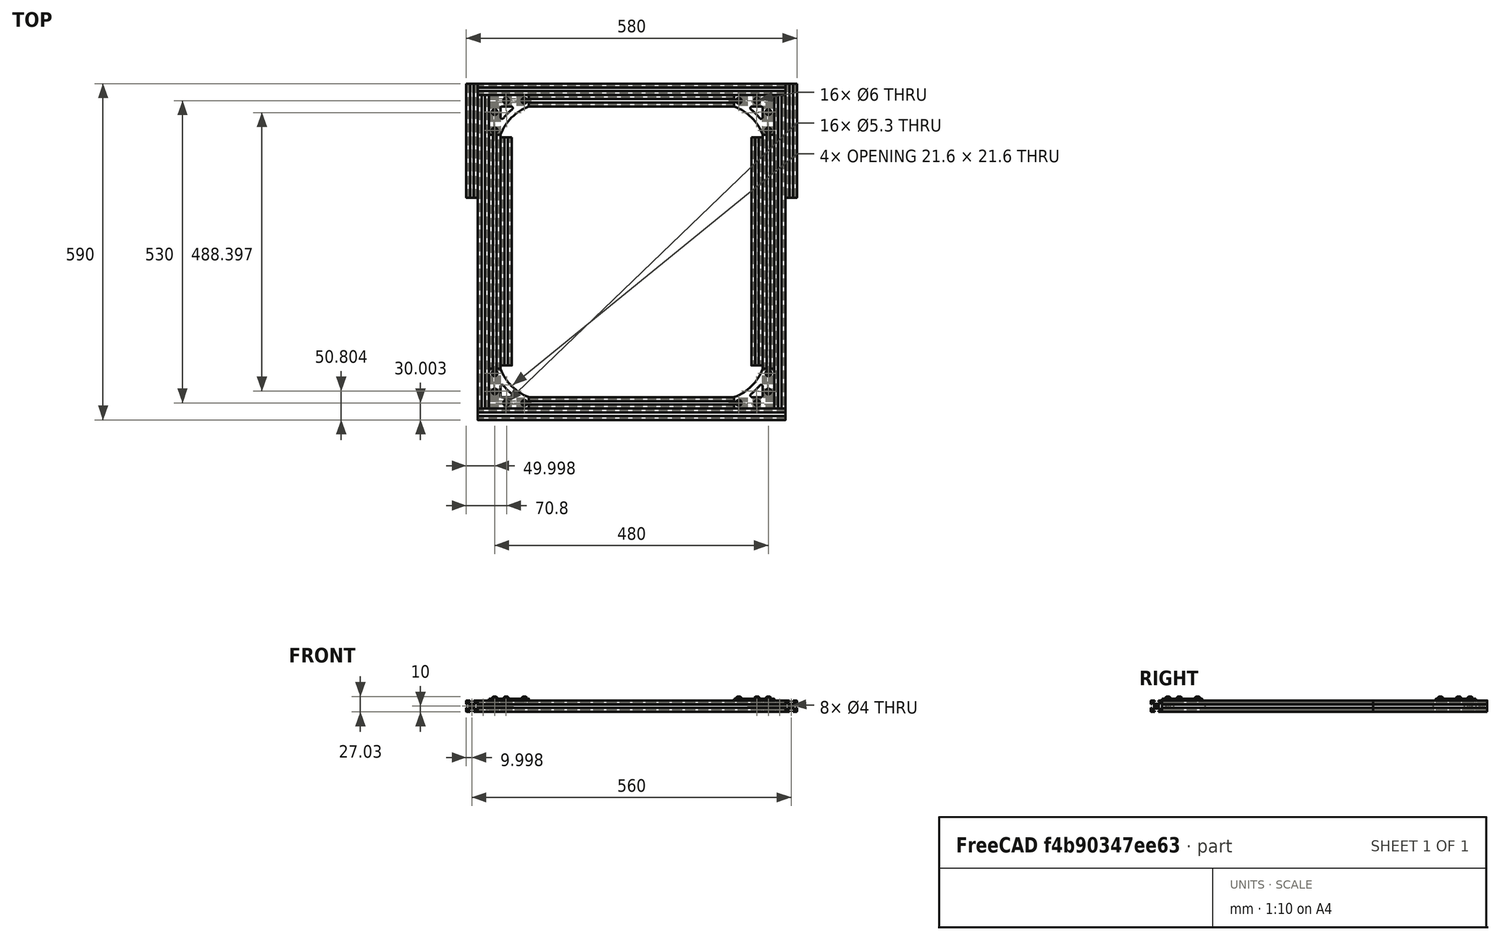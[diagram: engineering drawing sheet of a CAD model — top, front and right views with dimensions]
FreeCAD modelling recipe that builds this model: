
FCSTD DOCUMENT  (FreeCAD 0.17R7761 (Git))
Label: TAZ6_frame_assy_fixture
License: CreativeCommons Attribution-ShareAlike
LicenseURL: http://creativecommons.org/licenses/by-sa/4.0/
objects: App::FeaturePython×89, Part::FeaturePython×49, Spreadsheet::Sheet×1
note: 49 computed .brp shape members not serialized (recipe doc carries the construction recipe); baked Part::Feature solids carry a one-line shape summary decoded from their .brp

FEATURE [Part::FeaturePython] _00mm_extrusion_01  # a2plus imported part (geometry in sourceFile) (typed FeaturePython)
  Placement = pos=(17.428,58.3428,0) rot=(0.57735,0.57735,0.57735;2.0944rad)
  fixedPosition = true
  sourceFile = <userpath>/shared-j/devel/lulzbot/TAZ/Olive/production_parts/jigs/500mm_extrusion.fcstd
  timeLastImport = 1465231095
  updateColors = true
FEATURE [Part::FeaturePython] _10mm_extrusion_01  # a2plus imported part (geometry in sourceFile) (typed FeaturePython)
  Placement = pos=(7.42801,68.3428,0) rot=(1,0,0;1.5708rad)
  fixedPosition = false
  sourceFile = <userpath>/shared-j/devel/lulzbot/TAZ/Olive/production_parts/jigs/510mm_extrusion.fcstd
  timeLastImport = 1465230221
  updateColors = true
FEATURE [App::FeaturePython] planeConstraint01  # a2plus constraint (typed FeaturePython)
  Object1 = _10mm_extrusion_01
  Object2 = _00mm_extrusion_01
  SubElement1 = Face2
  SubElement2 = Face27
  Type = plane
  directionConstraint = 0
  offset = 0
FEATURE [App::FeaturePython] planeConstraint01_mirror  label="planeConstraint01_"  # a2plus constraint (typed FeaturePython)
  Object1 = _10mm_extrusion_01
  Object2 = _00mm_extrusion_01
  SubElement1 = Face2
  SubElement2 = Face27
  Type = plane
  directionConstraint = 0
  offset = 0
FEATURE [App::FeaturePython] planeConstraint02  # a2plus constraint (typed FeaturePython)
  Object1 = _00mm_extrusion_01
  Object2 = _10mm_extrusion_01
  SubElement1 = Face2
  SubElement2 = Face27
  Type = plane
  directionConstraint = 1
  offset = 0
FEATURE [App::FeaturePython] planeConstraint02_mirror  label="planeConstraint02_"  # a2plus constraint (typed FeaturePython)
  Object1 = _00mm_extrusion_01
  Object2 = _10mm_extrusion_01
  SubElement1 = Face2
  SubElement2 = Face27
  Type = plane
  directionConstraint = 1
  offset = 0
FEATURE [Part::FeaturePython] _10mm_extrusion_01001  # a2plus imported part (geometry in sourceFile) (typed FeaturePython)
  Placement = pos=(-472.572,68.3428,0) rot=(1,0,0;1.5708rad)
  fixedPosition = false
  sourceFile = <userpath>/shared-j/devel/lulzbot/TAZ/Olive/production_parts/jigs/510mm_extrusion.fcstd
  timeLastImport = 1465230221
  updateColors = true
FEATURE [App::FeaturePython] planeConstraint03  # a2plus constraint (typed FeaturePython)
  Object1 = _10mm_extrusion_01001
  Object2 = _00mm_extrusion_01
  SubElement1 = Face1
  SubElement2 = Face23
  Type = plane
  directionConstraint = 0
  offset = 0
FEATURE [App::FeaturePython] planeConstraint03_mirror  label="planeConstraint03_"  # a2plus constraint (typed FeaturePython)
  Object1 = _10mm_extrusion_01001
  Object2 = _00mm_extrusion_01
  SubElement1 = Face1
  SubElement2 = Face23
  Type = plane
  directionConstraint = 0
  offset = 0
FEATURE [App::FeaturePython] planeConstraint04  # a2plus constraint (typed FeaturePython)
  Object1 = _10mm_extrusion_01001
  Object2 = _00mm_extrusion_01
  SubElement1 = Face6
  SubElement2 = Face5
  Type = plane
  directionConstraint = 0
  offset = 0
FEATURE [App::FeaturePython] planeConstraint04_mirror  label="planeConstraint04_"  # a2plus constraint (typed FeaturePython)
  Object1 = _10mm_extrusion_01001
  Object2 = _00mm_extrusion_01
  SubElement1 = Face6
  SubElement2 = Face5
  Type = plane
  directionConstraint = 0
  offset = 0
FEATURE [App::FeaturePython] planeConstraint05  # a2plus constraint (typed FeaturePython)
  Object1 = _10mm_extrusion_01001
  Object2 = _00mm_extrusion_01
  SubElement1 = Face2
  SubElement2 = Face27
  Type = plane
  directionConstraint = 0
  offset = 0
FEATURE [App::FeaturePython] planeConstraint05_mirror  label="planeConstraint05_"  # a2plus constraint (typed FeaturePython)
  Object1 = _10mm_extrusion_01001
  Object2 = _00mm_extrusion_01
  SubElement1 = Face2
  SubElement2 = Face27
  Type = plane
  directionConstraint = 0
  offset = 0
FEATURE [Part::FeaturePython] _00mm_extrusion_01001  # a2plus imported part (geometry in sourceFile) (typed FeaturePython)
  Placement = pos=(17.428,588.343,0) rot=(0.57735,0.57735,0.57735;2.0944rad)
  fixedPosition = false
  sourceFile = <userpath>/shared-j/devel/lulzbot/TAZ/Olive/production_parts/jigs/500mm_extrusion.fcstd
  timeLastImport = 1465231095
  updateColors = true
FEATURE [App::FeaturePython] planeConstraint06  # a2plus constraint (typed FeaturePython)
  Object1 = _00mm_extrusion_01001
  Object2 = _10mm_extrusion_01001
  SubElement1 = Face5
  SubElement2 = Face26
  Type = plane
  directionConstraint = 0
  offset = 0
FEATURE [App::FeaturePython] planeConstraint06_mirror  label="planeConstraint06_"  # a2plus constraint (typed FeaturePython)
  Object1 = _00mm_extrusion_01001
  Object2 = _10mm_extrusion_01001
  SubElement1 = Face5
  SubElement2 = Face26
  Type = plane
  directionConstraint = 0
  offset = 0
FEATURE [App::FeaturePython] planeConstraint07  # a2plus constraint (typed FeaturePython)
  Object1 = _00mm_extrusion_01001
  Object2 = _10mm_extrusion_01001
  SubElement1 = Face6
  SubElement2 = Face5
  Type = plane
  directionConstraint = 1
  offset = 0
FEATURE [App::FeaturePython] planeConstraint07_mirror  label="planeConstraint07_"  # a2plus constraint (typed FeaturePython)
  Object1 = _00mm_extrusion_01001
  Object2 = _10mm_extrusion_01001
  SubElement1 = Face6
  SubElement2 = Face5
  Type = plane
  directionConstraint = 1
  offset = 0
FEATURE [App::FeaturePython] planeConstraint08  # a2plus constraint (typed FeaturePython)
  Object1 = _00mm_extrusion_01001
  Object2 = _10mm_extrusion_01001
  SubElement1 = Face1
  SubElement2 = Face23
  Type = plane
  directionConstraint = 0
  offset = 0
FEATURE [App::FeaturePython] planeConstraint08_mirror  label="planeConstraint08_"  # a2plus constraint (typed FeaturePython)
  Object1 = _00mm_extrusion_01001
  Object2 = _10mm_extrusion_01001
  SubElement1 = Face1
  SubElement2 = Face23
  Type = plane
  directionConstraint = 0
  offset = 0
FEATURE [Part::FeaturePython] muxedAssembly  label="TAZ6_frame_muxedAssembly"  # WARN: FeaturePython — macro-defined, semantics opaque (R4)
  type = muxedAssembly
FEATURE [Part::FeaturePython] _50mm_extrusion_01  # a2plus imported part (geometry in sourceFile) (typed FeaturePython)
  Placement = pos=(-492.572,48.3428,0) rot=(1,0,0;1.5708rad)
  fixedPosition = false
  sourceFile = <userpath>/shared-j/devel/lulzbot/TAZ/Olive/production_parts/jigs/550mm_extrusion.fcstd
  timeLastImport = 1465233027
  updateColors = true
FEATURE [App::FeaturePython] planeConstraint09  # a2plus constraint (typed FeaturePython)
  Object1 = _50mm_extrusion_01
  Object2 = muxedAssembly
  SubElement1 = Face23
  SubElement2 = Face23
  Type = plane
  directionConstraint = 0
  offset = 0
FEATURE [App::FeaturePython] planeConstraint09_mirror  label="planeConstraint09_"  # a2plus constraint (typed FeaturePython)
  Object1 = _50mm_extrusion_01
  Object2 = muxedAssembly
  SubElement1 = Face23
  SubElement2 = Face23
  Type = plane
  directionConstraint = 0
  offset = 0
FEATURE [App::FeaturePython] planeConstraint10  # a2plus constraint (typed FeaturePython)
  Object1 = _50mm_extrusion_01
  Object2 = muxedAssembly
  SubElement1 = Face2
  SubElement2 = Face6
  Type = plane
  directionConstraint = 1
  offset = 0
FEATURE [App::FeaturePython] planeConstraint10_mirror  label="planeConstraint10_"  # a2plus constraint (typed FeaturePython)
  Object1 = _50mm_extrusion_01
  Object2 = muxedAssembly
  SubElement1 = Face2
  SubElement2 = Face6
  Type = plane
  directionConstraint = 1
  offset = 0
FEATURE [App::FeaturePython] planeConstraint11  # a2plus constraint (typed FeaturePython)
  Object1 = _50mm_extrusion_01
  Object2 = muxedAssembly
  SubElement1 = Face47
  SubElement2 = Face108
  Type = plane
  directionConstraint = 1
  offset = 0
FEATURE [App::FeaturePython] planeConstraint11_mirror  label="planeConstraint11_"  # a2plus constraint (typed FeaturePython)
  Object1 = _50mm_extrusion_01
  Object2 = muxedAssembly
  SubElement1 = Face47
  SubElement2 = Face108
  Type = plane
  directionConstraint = 1
  offset = 0
FEATURE [Part::FeaturePython] _50mm_extrusion_01001  # a2plus imported part (geometry in sourceFile) (typed FeaturePython)
  Placement = pos=(27.428,598.343,0) rot=(0,0.707107,0.707107;3.14159rad)
  fixedPosition = false
  sourceFile = <userpath>/shared-j/devel/lulzbot/TAZ/Olive/production_parts/jigs/550mm_extrusion.fcstd
  timeLastImport = 1465233027
  updateColors = true
FEATURE [App::FeaturePython] planeConstraint12  # a2plus constraint (typed FeaturePython)
  Object1 = _50mm_extrusion_01001
  Object2 = muxedAssembly
  SubElement1 = Face23
  SubElement2 = Face74
  Type = plane
  directionConstraint = 0
  offset = 0
FEATURE [App::FeaturePython] planeConstraint12_mirror  label="planeConstraint12_"  # a2plus constraint (typed FeaturePython)
  Object1 = _50mm_extrusion_01001
  Object2 = muxedAssembly
  SubElement1 = Face23
  SubElement2 = Face74
  Type = plane
  directionConstraint = 0
  offset = 0
FEATURE [App::FeaturePython] planeConstraint13  # a2plus constraint (typed FeaturePython)
  Object1 = _50mm_extrusion_01001
  Object2 = muxedAssembly
  SubElement1 = Face47
  SubElement2 = Face98
  Type = plane
  directionConstraint = 1
  offset = 0
FEATURE [App::FeaturePython] planeConstraint13_mirror  label="planeConstraint13_"  # a2plus constraint (typed FeaturePython)
  Object1 = _50mm_extrusion_01001
  Object2 = muxedAssembly
  SubElement1 = Face47
  SubElement2 = Face98
  Type = plane
  directionConstraint = 1
  offset = 0
FEATURE [App::FeaturePython] planeConstraint14  # a2plus constraint (typed FeaturePython)
  Object1 = _50mm_extrusion_01001
  Object2 = muxedAssembly
  SubElement1 = Face2
  SubElement2 = Face200
  Type = plane
  directionConstraint = 1
  offset = 0
FEATURE [App::FeaturePython] planeConstraint14_mirror  label="planeConstraint14_"  # a2plus constraint (typed FeaturePython)
  Object1 = _50mm_extrusion_01001
  Object2 = muxedAssembly
  SubElement1 = Face2
  SubElement2 = Face200
  Type = plane
  directionConstraint = 1
  offset = 0
FEATURE [Part::FeaturePython] _40mm_extrusion_01  # a2plus imported part (geometry in sourceFile) (typed FeaturePython)
  Placement = pos=(37.428,38.3428,0) rot=(0.57735,0.57735,0.57735;2.0944rad)
  fixedPosition = false
  sourceFile = <userpath>/shared-j/devel/lulzbot/TAZ/Olive/production_parts/jigs/540mm_extrusion.fcstd
  timeLastImport = 1465233682
  updateColors = true
FEATURE [App::FeaturePython] planeConstraint15  # a2plus constraint (typed FeaturePython)
  Object1 = _40mm_extrusion_01
  Object2 = muxedAssembly
  SubElement1 = Face23
  SubElement2 = Face23
  Type = plane
  directionConstraint = 0
  offset = 0
FEATURE [App::FeaturePython] planeConstraint15_mirror  label="planeConstraint15_"  # a2plus constraint (typed FeaturePython)
  Object1 = _40mm_extrusion_01
  Object2 = muxedAssembly
  SubElement1 = Face23
  SubElement2 = Face23
  Type = plane
  directionConstraint = 0
  offset = 0
FEATURE [App::FeaturePython] planeConstraint16  # a2plus constraint (typed FeaturePython)
  Object1 = _40mm_extrusion_01
  Object2 = muxedAssembly
  SubElement1 = Face27
  SubElement2 = Face6
  Type = plane
  directionConstraint = 1
  offset = 0
FEATURE [App::FeaturePython] planeConstraint16_mirror  label="planeConstraint16_"  # a2plus constraint (typed FeaturePython)
  Object1 = _40mm_extrusion_01
  Object2 = muxedAssembly
  SubElement1 = Face27
  SubElement2 = Face6
  Type = plane
  directionConstraint = 1
  offset = 0
FEATURE [App::FeaturePython] planeConstraint17  # a2plus constraint (typed FeaturePython)
  Object1 = _40mm_extrusion_01
  Object2 = _50mm_extrusion_01
  SubElement1 = Face5
  SubElement2 = Face6
  Type = plane
  directionConstraint = 0
  offset = 0
FEATURE [App::FeaturePython] planeConstraint17_mirror  label="planeConstraint17_"  # a2plus constraint (typed FeaturePython)
  Object1 = _40mm_extrusion_01
  Object2 = _50mm_extrusion_01
  SubElement1 = Face5
  SubElement2 = Face6
  Type = plane
  directionConstraint = 0
  offset = 0
FEATURE [Part::FeaturePython] _40mm_extrusion_01001  # a2plus imported part (geometry in sourceFile) (typed FeaturePython)
  Placement = pos=(37.428,608.343,0) rot=(0.57735,0.57735,0.57735;2.0944rad)
  fixedPosition = false
  sourceFile = <userpath>/shared-j/devel/lulzbot/TAZ/Olive/production_parts/jigs/540mm_extrusion.fcstd
  timeLastImport = 1465233682
  updateColors = true
FEATURE [App::FeaturePython] planeConstraint18  # a2plus constraint (typed FeaturePython)
  Object1 = _40mm_extrusion_01001
  Object2 = _50mm_extrusion_01001
  SubElement1 = Face1
  SubElement2 = Face1
  Type = plane
  directionConstraint = 0
  offset = 0
FEATURE [App::FeaturePython] planeConstraint18_mirror  label="planeConstraint18_"  # a2plus constraint (typed FeaturePython)
  Object1 = _40mm_extrusion_01001
  Object2 = _50mm_extrusion_01001
  SubElement1 = Face1
  SubElement2 = Face1
  Type = plane
  directionConstraint = 0
  offset = 0
FEATURE [App::FeaturePython] planeConstraint19  # a2plus constraint (typed FeaturePython)
  Object1 = _40mm_extrusion_01001
  Object2 = _50mm_extrusion_01001
  SubElement1 = Face2
  SubElement2 = Face26
  Type = plane
  directionConstraint = 1
  offset = 0
FEATURE [App::FeaturePython] planeConstraint19_mirror  label="planeConstraint19_"  # a2plus constraint (typed FeaturePython)
  Object1 = _40mm_extrusion_01001
  Object2 = _50mm_extrusion_01001
  SubElement1 = Face2
  SubElement2 = Face26
  Type = plane
  directionConstraint = 1
  offset = 0
FEATURE [App::FeaturePython] planeConstraint20  # a2plus constraint (typed FeaturePython)
  Object1 = _40mm_extrusion_01001
  Object2 = _50mm_extrusion_01001
  SubElement1 = Face6
  SubElement2 = Face2
  Type = plane
  directionConstraint = 0
  offset = 0
FEATURE [App::FeaturePython] planeConstraint20_mirror  label="planeConstraint20_"  # a2plus constraint (typed FeaturePython)
  Object1 = _40mm_extrusion_01001
  Object2 = _50mm_extrusion_01001
  SubElement1 = Face6
  SubElement2 = Face2
  Type = plane
  directionConstraint = 0
  offset = 0
FEATURE [Part::FeaturePython] _00mm_extrusion_01002  # a2plus imported part (geometry in sourceFile) (typed FeaturePython)
  Placement = pos=(47.428,618.343,0) rot=(0,0.707107,0.707107;3.14159rad)
  fixedPosition = false
  sourceFile = <userpath>/shared-j/devel/lulzbot/TAZ/Olive/production_parts/jigs/200mm_extrusion.fcstd
  timeLastImport = 1465234395
  updateColors = true
FEATURE [App::FeaturePython] planeConstraint21  # a2plus constraint (typed FeaturePython)
  Object1 = _00mm_extrusion_01002
  Object2 = _40mm_extrusion_01001
  SubElement1 = Face50
  SubElement2 = Face50
  Type = plane
  directionConstraint = 0
  offset = 0
FEATURE [App::FeaturePython] planeConstraint21_mirror  label="planeConstraint21_"  # a2plus constraint (typed FeaturePython)
  Object1 = _00mm_extrusion_01002
  Object2 = _40mm_extrusion_01001
  SubElement1 = Face50
  SubElement2 = Face50
  Type = plane
  directionConstraint = 0
  offset = 0
FEATURE [App::FeaturePython] planeConstraint22  # a2plus constraint (typed FeaturePython)
  Object1 = _00mm_extrusion_01002
  Object2 = _40mm_extrusion_01001
  SubElement1 = Face2
  SubElement2 = Face27
  Type = plane
  directionConstraint = 1
  offset = 0
FEATURE [App::FeaturePython] planeConstraint22_mirror  label="planeConstraint22_"  # a2plus constraint (typed FeaturePython)
  Object1 = _00mm_extrusion_01002
  Object2 = _40mm_extrusion_01001
  SubElement1 = Face2
  SubElement2 = Face27
  Type = plane
  directionConstraint = 1
  offset = 0
FEATURE [App::FeaturePython] planeConstraint23  # a2plus constraint (typed FeaturePython)
  Object1 = _00mm_extrusion_01002
  Object2 = _50mm_extrusion_01001
  SubElement1 = Face27
  SubElement2 = Face26
  Type = plane
  directionConstraint = 0
  offset = 0
FEATURE [App::FeaturePython] planeConstraint23_mirror  label="planeConstraint23_"  # a2plus constraint (typed FeaturePython)
  Object1 = _00mm_extrusion_01002
  Object2 = _50mm_extrusion_01001
  SubElement1 = Face27
  SubElement2 = Face26
  Type = plane
  directionConstraint = 0
  offset = 0
FEATURE [Part::FeaturePython] _00mm_extrusion_01003  # a2plus imported part (geometry in sourceFile) (typed FeaturePython)
  Placement = pos=(-512.572,418.343,0) rot=(1,0,0;1.5708rad)
  fixedPosition = false
  sourceFile = <userpath>/shared-j/devel/lulzbot/TAZ/Olive/production_parts/jigs/200mm_extrusion.fcstd
  timeLastImport = 1465234395
  updateColors = true
FEATURE [App::FeaturePython] planeConstraint24  # a2plus constraint (typed FeaturePython)
  Object1 = _00mm_extrusion_01003
  Object2 = _50mm_extrusion_01
  SubElement1 = Face50
  SubElement2 = Face30
  Type = plane
  directionConstraint = 0
  offset = 0
FEATURE [App::FeaturePython] planeConstraint24_mirror  label="planeConstraint24_"  # a2plus constraint (typed FeaturePython)
  Object1 = _00mm_extrusion_01003
  Object2 = _50mm_extrusion_01
  SubElement1 = Face50
  SubElement2 = Face30
  Type = plane
  directionConstraint = 0
  offset = 0
FEATURE [App::FeaturePython] planeConstraint25  # a2plus constraint (typed FeaturePython)
  Object1 = _00mm_extrusion_01003
  Object2 = _40mm_extrusion_01001
  SubElement1 = Face5
  SubElement2 = Face27
  Type = plane
  directionConstraint = 0
  offset = 0
FEATURE [App::FeaturePython] planeConstraint25_mirror  label="planeConstraint25_"  # a2plus constraint (typed FeaturePython)
  Object1 = _00mm_extrusion_01003
  Object2 = _40mm_extrusion_01001
  SubElement1 = Face5
  SubElement2 = Face27
  Type = plane
  directionConstraint = 0
  offset = 0
FEATURE [App::FeaturePython] planeConstraint26  # a2plus constraint (typed FeaturePython)
  Object1 = _00mm_extrusion_01003
  Object2 = _50mm_extrusion_01
  SubElement1 = Face47
  SubElement2 = Face26
  Type = plane
  directionConstraint = 0
  offset = 0
FEATURE [App::FeaturePython] planeConstraint26_mirror  label="planeConstraint26_"  # a2plus constraint (typed FeaturePython)
  Object1 = _00mm_extrusion_01003
  Object2 = _50mm_extrusion_01
  SubElement1 = Face47
  SubElement2 = Face26
  Type = plane
  directionConstraint = 0
  offset = 0
FEATURE [Part::FeaturePython] _00mm_extrusion_01004  # a2plus imported part (geometry in sourceFile) (typed FeaturePython)
  Placement = pos=(-12.572,523.9,0) rot=(0,0.707107,0.707107;3.14159rad)
  fixedPosition = false
  sourceFile = <userpath>/shared-j/devel/lulzbot/TAZ/Olive/production_parts/jigs/400mm_extrusion.fcstd
  timeLastImport = 1465243496
  updateColors = true
FEATURE [App::FeaturePython] planeConstraint27  # a2plus constraint (typed FeaturePython)
  Object1 = _00mm_extrusion_01004
  Object2 = _50mm_extrusion_01001
  SubElement1 = Face50
  SubElement2 = Face50
  Type = plane
  directionConstraint = 0
  offset = 0
FEATURE [App::FeaturePython] planeConstraint27_mirror  label="planeConstraint27_"  # a2plus constraint (typed FeaturePython)
  Object1 = _00mm_extrusion_01004
  Object2 = _50mm_extrusion_01001
  SubElement1 = Face50
  SubElement2 = Face50
  Type = plane
  directionConstraint = 0
  offset = 0
FEATURE [App::FeaturePython] planeConstraint28  # a2plus constraint (typed FeaturePython)
  Object1 = _00mm_extrusion_01004
  Object2 = muxedAssembly
  SubElement1 = Face26
  SubElement2 = Face77
  Type = plane
  directionConstraint = 1
  offset = 0
FEATURE [App::FeaturePython] planeConstraint28_mirror  label="planeConstraint28_"  # a2plus constraint (typed FeaturePython)
  Object1 = _00mm_extrusion_01004
  Object2 = muxedAssembly
  SubElement1 = Face26
  SubElement2 = Face77
  Type = plane
  directionConstraint = 1
  offset = 0
FEATURE [Part::FeaturePython] _00mm_extrusion_01005  # a2plus imported part (geometry in sourceFile) (typed FeaturePython)
  Placement = pos=(-452.572,123.9,0) rot=(1,0,0;1.5708rad)
  fixedPosition = false
  sourceFile = <userpath>/shared-j/devel/lulzbot/TAZ/Olive/production_parts/jigs/400mm_extrusion.fcstd
  timeLastImport = 1465243496
  updateColors = true
FEATURE [App::FeaturePython] planeConstraint29  # a2plus constraint (typed FeaturePython)
  Object1 = _00mm_extrusion_01005
  Object2 = _50mm_extrusion_01
  SubElement1 = Face23
  SubElement2 = Face23
  Type = plane
  directionConstraint = 0
  offset = 0
FEATURE [App::FeaturePython] planeConstraint29_mirror  label="planeConstraint29_"  # a2plus constraint (typed FeaturePython)
  Object1 = _00mm_extrusion_01005
  Object2 = _50mm_extrusion_01
  SubElement1 = Face23
  SubElement2 = Face23
  Type = plane
  directionConstraint = 0
  offset = 0
FEATURE [App::FeaturePython] planeConstraint30  # a2plus constraint (typed FeaturePython)
  Object1 = _00mm_extrusion_01005
  Object2 = muxedAssembly
  SubElement1 = Face6
  SubElement2 = Face129
  Type = plane
  directionConstraint = 1
  offset = 0
FEATURE [App::FeaturePython] planeConstraint30_mirror  label="planeConstraint30_"  # a2plus constraint (typed FeaturePython)
  Object1 = _00mm_extrusion_01005
  Object2 = muxedAssembly
  SubElement1 = Face6
  SubElement2 = Face129
  Type = plane
  directionConstraint = 1
  offset = 0
FEATURE [App::FeaturePython] planeConstraint31  # a2plus constraint (typed FeaturePython)
  Object1 = _00mm_extrusion_01005
  Object2 = _00mm_extrusion_01004
  SubElement1 = Face2
  SubElement2 = Face5
  Type = plane
  directionConstraint = 0
  offset = 0
FEATURE [App::FeaturePython] planeConstraint31_mirror  label="planeConstraint31_"  # a2plus constraint (typed FeaturePython)
  Object1 = _00mm_extrusion_01005
  Object2 = _00mm_extrusion_01004
  SubElement1 = Face2
  SubElement2 = Face5
  Type = plane
  directionConstraint = 0
  offset = 0
FEATURE [Part::FeaturePython] corner_bracket_v2_0_PP_MP0106_step1_01  # a2plus imported part (geometry in sourceFile) (typed FeaturePython)
  Placement = pos=(-482.572,118.343,13.175) rot=(1,0,0;1.5708rad)
  fixedPosition = false
  sourceFile = <userpath>/shared-j/devel/lulzbot/TAZ/Olive/production_parts/machined_parts/corner_bracket_v2.0/corner_bracket_v2.0_PP-MP0106.step
  timeLastImport = 1441125151
  updateColors = true
FEATURE [App::FeaturePython] planeConstraint32  # a2plus constraint (typed FeaturePython)
  Object1 = corner_bracket_v2_0_PP_MP0106_step1_01
  Object2 = muxedAssembly
  SubElement1 = Face22
  SubElement2 = Face103
  Type = plane
  directionConstraint = 1
  offset = 0
FEATURE [App::FeaturePython] planeConstraint32_mirror  label="planeConstraint32_"  # a2plus constraint (typed FeaturePython)
  Object1 = corner_bracket_v2_0_PP_MP0106_step1_01
  Object2 = muxedAssembly
  SubElement1 = Face22
  SubElement2 = Face103
  Type = plane
  directionConstraint = 1
  offset = 0
FEATURE [App::FeaturePython] planeConstraint33  # a2plus constraint (typed FeaturePython)
  Object1 = corner_bracket_v2_0_PP_MP0106_step1_01
  Object2 = muxedAssembly
  SubElement1 = Face6
  SubElement2 = Face6
  Type = plane
  directionConstraint = 0
  offset = 0
FEATURE [App::FeaturePython] planeConstraint33_mirror  label="planeConstraint33_"  # a2plus constraint (typed FeaturePython)
  Object1 = corner_bracket_v2_0_PP_MP0106_step1_01
  Object2 = muxedAssembly
  SubElement1 = Face6
  SubElement2 = Face6
  Type = plane
  directionConstraint = 0
  offset = 0
FEATURE [App::FeaturePython] planeConstraint34  # a2plus constraint (typed FeaturePython)
  Object1 = corner_bracket_v2_0_PP_MP0106_step1_01
  Object2 = muxedAssembly
  SubElement1 = Face10
  SubElement2 = Face108
  Type = plane
  directionConstraint = 0
  offset = 0
FEATURE [App::FeaturePython] planeConstraint34_mirror  label="planeConstraint34_"  # a2plus constraint (typed FeaturePython)
  Object1 = corner_bracket_v2_0_PP_MP0106_step1_01
  Object2 = muxedAssembly
  SubElement1 = Face10
  SubElement2 = Face108
  Type = plane
  directionConstraint = 0
  offset = 0
FEATURE [Part::FeaturePython] corner_bracket_v2_0_PP_MP0106_step1_01001  # a2plus imported part (geometry in sourceFile) (typed FeaturePython)
  Placement = pos=(-52.572,48.3428,13.175) rot=(0.57735,0.57735,0.57735;2.0944rad)
  fixedPosition = false
  sourceFile = <userpath>/shared-j/devel/lulzbot/TAZ/Olive/production_parts/machined_parts/corner_bracket_v2.0/corner_bracket_v2.0_PP-MP0106.step
  timeLastImport = 1441125151
  updateColors = true
FEATURE [App::FeaturePython] planeConstraint35  # a2plus constraint (typed FeaturePython)
  Object1 = corner_bracket_v2_0_PP_MP0106_step1_01001
  Object2 = muxedAssembly
  SubElement1 = Face22
  SubElement2 = Face1
  Type = plane
  directionConstraint = 1
  offset = 0
FEATURE [App::FeaturePython] planeConstraint35_mirror  label="planeConstraint35_"  # a2plus constraint (typed FeaturePython)
  Object1 = corner_bracket_v2_0_PP_MP0106_step1_01001
  Object2 = muxedAssembly
  SubElement1 = Face22
  SubElement2 = Face1
  Type = plane
  directionConstraint = 1
  offset = 0
FEATURE [App::FeaturePython] planeConstraint36  # a2plus constraint (typed FeaturePython)
  Object1 = corner_bracket_v2_0_PP_MP0106_step1_01001
  Object2 = muxedAssembly
  SubElement1 = Face10
  SubElement2 = Face6
  Type = plane
  directionConstraint = 0
  offset = 0
FEATURE [App::FeaturePython] planeConstraint36_mirror  label="planeConstraint36_"  # a2plus constraint (typed FeaturePython)
  Object1 = corner_bracket_v2_0_PP_MP0106_step1_01001
  Object2 = muxedAssembly
  SubElement1 = Face10
  SubElement2 = Face6
  Type = plane
  directionConstraint = 0
  offset = 0
FEATURE [App::FeaturePython] planeConstraint37  # a2plus constraint (typed FeaturePython)
  Object1 = corner_bracket_v2_0_PP_MP0106_step1_01001
  Object2 = muxedAssembly
  SubElement1 = Face6
  SubElement2 = Face78
  Type = plane
  directionConstraint = 0
  offset = 0
FEATURE [App::FeaturePython] planeConstraint37_mirror  label="planeConstraint37_"  # a2plus constraint (typed FeaturePython)
  Object1 = corner_bracket_v2_0_PP_MP0106_step1_01001
  Object2 = muxedAssembly
  SubElement1 = Face6
  SubElement2 = Face78
  Type = plane
  directionConstraint = 0
  offset = 0
FEATURE [Part::FeaturePython] corner_bracket_v2_0_PP_MP0106_step1_01002  # a2plus imported part (geometry in sourceFile) (typed FeaturePython)
  Placement = pos=(-52.572,598.343,10) rot=(-0.57735,0.57735,-0.57735;2.0944rad)
  fixedPosition = false
  sourceFile = <userpath>/shared-j/devel/lulzbot/TAZ/Olive/production_parts/machined_parts/corner_bracket_v2.0/corner_bracket_v2.0_PP-MP0106.step
  timeLastImport = 1441125151
  updateColors = true
FEATURE [App::FeaturePython] planeConstraint38  # a2plus constraint (typed FeaturePython)
  Object1 = corner_bracket_v2_0_PP_MP0106_step1_01002
  Object2 = muxedAssembly
  SubElement1 = Face1
  SubElement2 = Face74
  Type = plane
  directionConstraint = 0
  offset = 0
FEATURE [App::FeaturePython] planeConstraint38_mirror  label="planeConstraint38_"  # a2plus constraint (typed FeaturePython)
  Object1 = corner_bracket_v2_0_PP_MP0106_step1_01002
  Object2 = muxedAssembly
  SubElement1 = Face1
  SubElement2 = Face74
  Type = plane
  directionConstraint = 0
  offset = 0
FEATURE [App::FeaturePython] planeConstraint39  # a2plus constraint (typed FeaturePython)
  Object1 = corner_bracket_v2_0_PP_MP0106_step1_01002
  Object2 = muxedAssembly
  SubElement1 = Face6
  SubElement2 = Face78
  Type = plane
  directionConstraint = 0
  offset = 0
FEATURE [App::FeaturePython] planeConstraint39_mirror  label="planeConstraint39_"  # a2plus constraint (typed FeaturePython)
  Object1 = corner_bracket_v2_0_PP_MP0106_step1_01002
  Object2 = muxedAssembly
  SubElement1 = Face6
  SubElement2 = Face78
  Type = plane
  directionConstraint = 0
  offset = 0
FEATURE [App::FeaturePython] planeConstraint40  # a2plus constraint (typed FeaturePython)
  Object1 = corner_bracket_v2_0_PP_MP0106_step1_01002
  Object2 = muxedAssembly
  SubElement1 = Face10
  SubElement2 = Face180
  Type = plane
  directionConstraint = 0
  offset = 0
FEATURE [App::FeaturePython] planeConstraint40_mirror  label="planeConstraint40_"  # a2plus constraint (typed FeaturePython)
  Object1 = corner_bracket_v2_0_PP_MP0106_step1_01002
  Object2 = muxedAssembly
  SubElement1 = Face10
  SubElement2 = Face180
  Type = plane
  directionConstraint = 0
  offset = 0
FEATURE [Part::FeaturePython] corner_bracket_v2_0_PP_MP0106_step1_01003  # a2plus imported part (geometry in sourceFile) (typed FeaturePython)
  Placement = pos=(-482.572,528.343,10) rot=(-1,0,0;1.5708rad)
  fixedPosition = false
  sourceFile = <userpath>/shared-j/devel/lulzbot/TAZ/Olive/production_parts/machined_parts/corner_bracket_v2.0/corner_bracket_v2.0_PP-MP0106.step
  timeLastImport = 1441125151
  updateColors = true
FEATURE [App::FeaturePython] planeConstraint41  # a2plus constraint (typed FeaturePython)
  Object1 = corner_bracket_v2_0_PP_MP0106_step1_01003
  Object2 = muxedAssembly
  SubElement1 = Face1
  SubElement2 = Face154
  Type = plane
  directionConstraint = 0
  offset = 0
FEATURE [App::FeaturePython] planeConstraint41_mirror  label="planeConstraint41_"  # a2plus constraint (typed FeaturePython)
  Object1 = corner_bracket_v2_0_PP_MP0106_step1_01003
  Object2 = muxedAssembly
  SubElement1 = Face1
  SubElement2 = Face154
  Type = plane
  directionConstraint = 0
  offset = 0
FEATURE [App::FeaturePython] planeConstraint42  # a2plus constraint (typed FeaturePython)
  Object1 = corner_bracket_v2_0_PP_MP0106_step1_01003
  Object2 = muxedAssembly
  SubElement1 = Face6
  SubElement2 = Face180
  Type = plane
  directionConstraint = 0
  offset = 0
FEATURE [App::FeaturePython] planeConstraint42_mirror  label="planeConstraint42_"  # a2plus constraint (typed FeaturePython)
  Object1 = corner_bracket_v2_0_PP_MP0106_step1_01003
  Object2 = muxedAssembly
  SubElement1 = Face6
  SubElement2 = Face180
  Type = plane
  directionConstraint = 0
  offset = 0
FEATURE [App::FeaturePython] planeConstraint43  # a2plus constraint (typed FeaturePython)
  Object1 = corner_bracket_v2_0_PP_MP0106_step1_01003
  Object2 = muxedAssembly
  SubElement1 = Face10
  SubElement2 = Face108
  Type = plane
  directionConstraint = 0
  offset = 0
FEATURE [App::FeaturePython] planeConstraint43_mirror  label="planeConstraint43_"  # a2plus constraint (typed FeaturePython)
  Object1 = corner_bracket_v2_0_PP_MP0106_step1_01003
  Object2 = muxedAssembly
  SubElement1 = Face10
  SubElement2 = Face108
  Type = plane
  directionConstraint = 0
  offset = 0
FEATURE [App::FeaturePython] axialConstraint01  # a2plus constraint (typed FeaturePython)
  Object1 = Screw
  Object2 = corner_bracket_v2_0_PP_MP0106_step1_01001
  SubElement1 = Face5
  SubElement2 = Face20
  Type = axial
  directionConstraint = 1
  lockRotation = false
FEATURE [App::FeaturePython] axialConstraint01_mirror  label="axialConstraint01_"  # a2plus constraint (typed FeaturePython)
  Object1 = Screw
  Object2 = corner_bracket_v2_0_PP_MP0106_step1_01001
  SubElement1 = Face5
  SubElement2 = Face20
  Type = axial
  directionConstraint = 1
  lockRotation = false
FEATURE [App::FeaturePython] axialConstraint02  # a2plus constraint (typed FeaturePython)
  Object1 = Washer
  Object2 = Screw
  SubElement1 = Face2
  SubElement2 = Face5
  Type = axial
  directionConstraint = 0
  lockRotation = false
FEATURE [Part::FeaturePython] Washer001  label="M5-Washer001"  # Fasteners workbench fastener (typed FeaturePython)
  Placement = pos=(-12.572,58.3428,13.175) rot=(0,0,1;0rad)
  baseObject = -> corner_bracket_v2_0_PP_MP0106_step1_01001 [Edge20]
  diameter = 6
  invert = true
  matchOuter = false
  offset = 0
  type = 0
FEATURE [Part::FeaturePython] Screw001  label="M5x10-Screw001"  # Fasteners workbench fastener (typed FeaturePython)
  Placement = pos=(-12.572,58.3428,14.275) rot=(0,0,1;0rad)
  baseObject = -> Washer001 [Edge1]
  diameter = 3
  invert = false
  length = 1
  matchOuter = false
  offset = 0
  thread = false
  type = 20
FEATURE [Part::FeaturePython] Washer  label="M5-Washer"  # Fasteners workbench fastener (typed FeaturePython)
  Placement = pos=(-44.572,58.3428,13.175) rot=(0,0,1;0rad)
  baseObject = -> corner_bracket_v2_0_PP_MP0106_step1_01001 [Edge19]
  diameter = 6
  invert = true
  matchOuter = false
  offset = 0
  type = 0
FEATURE [Part::FeaturePython] Screw  label="M5x10-Screw"  # Fasteners workbench fastener (typed FeaturePython)
  Placement = pos=(-44.572,58.3428,14.275) rot=(0,0,1;0rad)
  baseObject = -> Washer [Edge1]
  diameter = 3
  invert = false
  length = 1
  matchOuter = false
  offset = 0
  thread = false
  type = 20
FEATURE [Part::FeaturePython] Washer002  label="M5-Washer002"  # Fasteners workbench fastener (typed FeaturePython)
  Placement = pos=(7.42801,78.3428,13.175) rot=(0,0,1;0rad)
  baseObject = -> corner_bracket_v2_0_PP_MP0106_step1_01001 [Edge18]
  diameter = 6
  invert = true
  matchOuter = false
  offset = 0
  type = 0
FEATURE [Part::FeaturePython] Screw002  label="M5x10-Screw002"  # Fasteners workbench fastener (typed FeaturePython)
  Placement = pos=(7.42801,78.3428,14.275) rot=(0,0,1;0rad)
  baseObject = -> Washer002 [Edge1]
  diameter = 3
  invert = false
  length = 1
  matchOuter = false
  offset = 0
  thread = false
  type = 20
FEATURE [Part::FeaturePython] Washer003  label="M5-Washer003"  # Fasteners workbench fastener (typed FeaturePython)
  Placement = pos=(7.42801,110.343,13.175) rot=(0,0,1;0rad)
  baseObject = -> corner_bracket_v2_0_PP_MP0106_step1_01001 [Edge17]
  diameter = 6
  invert = true
  matchOuter = false
  offset = 0
  type = 0
FEATURE [Part::FeaturePython] Screw003  label="M5x10-Screw003"  # Fasteners workbench fastener (typed FeaturePython)
  Placement = pos=(7.42801,110.343,14.275) rot=(0,0,1;0rad)
  baseObject = -> Washer003 [Edge1]
  diameter = 3
  invert = false
  length = 1
  matchOuter = false
  offset = 0
  thread = false
  type = 20
FEATURE [Part::FeaturePython] Washer005  label="M5-Washer005"  # Fasteners workbench fastener (typed FeaturePython)
  Placement = pos=(7.42801,568.343,13.175) rot=(0,0,1;0rad)
  baseObject = -> corner_bracket_v2_0_PP_MP0106_step1_01002 [Edge56]
  diameter = 6
  invert = false
  matchOuter = false
  offset = 0
  type = 0
FEATURE [Part::FeaturePython] Screw005  label="M5x10-Screw005"  # Fasteners workbench fastener (typed FeaturePython)
  Placement = pos=(7.42801,568.343,14.275) rot=(0,0,1;0rad)
  baseObject = -> Washer005 [Edge1]
  diameter = 3
  invert = false
  length = 1
  matchOuter = false
  offset = 0
  thread = false
  type = 20
FEATURE [Part::FeaturePython] Washer006  label="M5-Washer006"  # Fasteners workbench fastener (typed FeaturePython)
  Placement = pos=(-12.572,588.343,13.175) rot=(0,0,1;0rad)
  baseObject = -> corner_bracket_v2_0_PP_MP0106_step1_01002 [Edge60]
  diameter = 6
  invert = false
  matchOuter = false
  offset = 0
  type = 0
FEATURE [Part::FeaturePython] Screw006  label="M5x10-Screw006"  # Fasteners workbench fastener (typed FeaturePython)
  Placement = pos=(-12.572,588.343,14.275) rot=(0,0,1;0rad)
  baseObject = -> Washer006 [Edge1]
  diameter = 3
  invert = false
  length = 1
  matchOuter = false
  offset = 0
  thread = false
  type = 20
FEATURE [Part::FeaturePython] Washer007  label="M5-Washer007"  # Fasteners workbench fastener (typed FeaturePython)
  Placement = pos=(-44.572,588.343,13.175) rot=(0,0,1;0rad)
  baseObject = -> corner_bracket_v2_0_PP_MP0106_step1_01002 [Edge58]
  diameter = 6
  invert = false
  matchOuter = false
  offset = 0
  type = 0
FEATURE [Part::FeaturePython] Screw007  label="M5x10-Screw007"  # Fasteners workbench fastener (typed FeaturePython)
  Placement = pos=(-44.572,588.343,14.275) rot=(0,0,1;0rad)
  baseObject = -> Washer007 [Edge1]
  diameter = 3
  invert = false
  length = 1
  matchOuter = false
  offset = 0
  thread = false
  type = 20
FEATURE [Part::FeaturePython] Washer008  label="M5-Washer008"  # Fasteners workbench fastener (typed FeaturePython)
  Placement = pos=(-420.572,588.343,13.175) rot=(0,0,1;0rad)
  baseObject = -> corner_bracket_v2_0_PP_MP0106_step1_01003 [Edge54]
  diameter = 6
  invert = false
  matchOuter = false
  offset = 0
  type = 0
FEATURE [Part::FeaturePython] Washer009  label="M5-Washer009"  # Fasteners workbench fastener (typed FeaturePython)
  Placement = pos=(-452.572,588.343,13.175) rot=(0,0,1;0rad)
  baseObject = -> corner_bracket_v2_0_PP_MP0106_step1_01003 [Edge56]
  diameter = 6
  invert = false
  matchOuter = false
  offset = 0
  type = 0
FEATURE [Part::FeaturePython] Washer010  label="M5-Washer010"  # Fasteners workbench fastener (typed FeaturePython)
  Placement = pos=(-472.572,568.343,13.175) rot=(0,0,1;0rad)
  baseObject = -> corner_bracket_v2_0_PP_MP0106_step1_01003 [Edge60]
  diameter = 6
  invert = false
  matchOuter = false
  offset = 0
  type = 0
FEATURE [Part::FeaturePython] Washer011  label="M5-Washer011"  # Fasteners workbench fastener (typed FeaturePython)
  Placement = pos=(-472.572,536.343,13.175) rot=(0,0,1;0rad)
  baseObject = -> corner_bracket_v2_0_PP_MP0106_step1_01003 [Edge58]
  diameter = 6
  invert = false
  matchOuter = false
  offset = 0
  type = 0
FEATURE [Part::FeaturePython] Screw008  label="M5x10-Screw008"  # Fasteners workbench fastener (typed FeaturePython)
  Placement = pos=(-420.572,588.343,14.275) rot=(0,0,1;0rad)
  baseObject = -> Washer008 [Edge1]
  diameter = 3
  invert = false
  length = 1
  matchOuter = false
  offset = 0
  thread = false
  type = 20
FEATURE [Part::FeaturePython] Screw009  label="M5x10-Screw009"  # Fasteners workbench fastener (typed FeaturePython)
  Placement = pos=(-452.572,588.343,14.275) rot=(0,0,1;0rad)
  baseObject = -> Washer009 [Edge1]
  diameter = 3
  invert = false
  length = 1
  matchOuter = false
  offset = 0
  thread = false
  type = 20
FEATURE [Part::FeaturePython] Screw010  label="M5x10-Screw010"  # Fasteners workbench fastener (typed FeaturePython)
  Placement = pos=(-472.572,568.343,14.275) rot=(0,0,1;0rad)
  baseObject = -> Washer010 [Edge1]
  diameter = 3
  invert = false
  length = 1
  matchOuter = false
  offset = 0
  thread = false
  type = 20
FEATURE [Part::FeaturePython] Screw011  label="M5x10-Screw011"  # Fasteners workbench fastener (typed FeaturePython)
  Placement = pos=(-472.572,536.343,14.275) rot=(0,0,1;0rad)
  baseObject = -> Washer011 [Edge1]
  diameter = 3
  invert = false
  length = 1
  matchOuter = false
  offset = 0
  thread = false
  type = 20
FEATURE [Part::FeaturePython] Washer012  label="M5-Washer012"  # Fasteners workbench fastener (typed FeaturePython)
  Placement = pos=(-472.572,110.343,13.175) rot=(0,0,1;0rad)
  baseObject = -> corner_bracket_v2_0_PP_MP0106_step1_01 [Edge19]
  diameter = 6
  invert = true
  matchOuter = false
  offset = 0
  type = 0
FEATURE [Part::FeaturePython] Washer013  label="M5-Washer013"  # Fasteners workbench fastener (typed FeaturePython)
  Placement = pos=(-472.572,78.3428,13.175) rot=(0,0,1;0rad)
  baseObject = -> corner_bracket_v2_0_PP_MP0106_step1_01 [Edge20]
  diameter = 6
  invert = true
  matchOuter = false
  offset = 0
  type = 0
FEATURE [Part::FeaturePython] Washer014  label="M5-Washer014"  # Fasteners workbench fastener (typed FeaturePython)
  Placement = pos=(-452.572,58.3428,13.175) rot=(0,0,1;0rad)
  baseObject = -> corner_bracket_v2_0_PP_MP0106_step1_01 [Edge18]
  diameter = 6
  invert = true
  matchOuter = false
  offset = 0
  type = 0
FEATURE [Part::FeaturePython] Washer015  label="M5-Washer015"  # Fasteners workbench fastener (typed FeaturePython)
  Placement = pos=(-420.572,58.3428,13.175) rot=(0,0,1;0rad)
  baseObject = -> corner_bracket_v2_0_PP_MP0106_step1_01 [Edge17]
  diameter = 6
  invert = true
  matchOuter = false
  offset = 0
  type = 0
FEATURE [Part::FeaturePython] Screw012  label="M5x10-Screw015"  # Fasteners workbench fastener (typed FeaturePython)
  Placement = pos=(-420.572,58.3428,14.275) rot=(0,0,1;0rad)
  baseObject = -> Washer015 [Edge1]
  diameter = 3
  invert = false
  length = 1
  matchOuter = false
  offset = 0
  thread = false
  type = 20
FEATURE [Part::FeaturePython] Screw013  label="M5x10-Screw014"  # Fasteners workbench fastener (typed FeaturePython)
  Placement = pos=(-452.572,58.3428,14.275) rot=(0,0,1;0rad)
  baseObject = -> Washer014 [Edge1]
  diameter = 3
  invert = false
  length = 1
  matchOuter = false
  offset = 0
  thread = false
  type = 20
FEATURE [Part::FeaturePython] Screw014  label="M5x10-Screw013"  # Fasteners workbench fastener (typed FeaturePython)
  Placement = pos=(-472.572,78.3428,14.275) rot=(0,0,1;0rad)
  baseObject = -> Washer013 [Edge1]
  diameter = 3
  invert = false
  length = 1
  matchOuter = false
  offset = 0
  thread = false
  type = 20
FEATURE [Part::FeaturePython] Screw015  label="M5x10-Screw012"  # Fasteners workbench fastener (typed FeaturePython)
  Placement = pos=(-472.572,110.343,14.275) rot=(0,0,1;0rad)
  baseObject = -> Washer012 [Edge1]
  diameter = 3
  invert = false
  length = 1
  matchOuter = false
  offset = 0
  thread = false
  type = 20
FEATURE [Spreadsheet::Sheet] Fasteners_BOM
  cells = A1=Type; B1=Qty; A2=ISO7089 Washer M5; B2=16; A3=ISO7380-1 Screw M5x10; B3=16
FEATURE [Part::FeaturePython] Washer016  label="M5-Washer016"  # Fasteners workbench fastener (typed FeaturePython)
  Placement = pos=(7.42801,536.343,13.175) rot=(0,0,1;0rad)
  baseObject = -> corner_bracket_v2_0_PP_MP0106_step1_01002 [Edge54]
  diameter = 6
  invert = false
  matchOuter = false
  offset = 0
  type = 0
FEATURE [Part::FeaturePython] Screw016  label="M5x10-Screw016"  # Fasteners workbench fastener (typed FeaturePython)
  Placement = pos=(7.42801,536.343,14.275) rot=(0,0,1;0rad)
  baseObject = -> Washer016 [Edge1]
  diameter = 3
  invert = false
  length = 1
  matchOuter = false
  offset = 0
  thread = false
  type = 20
